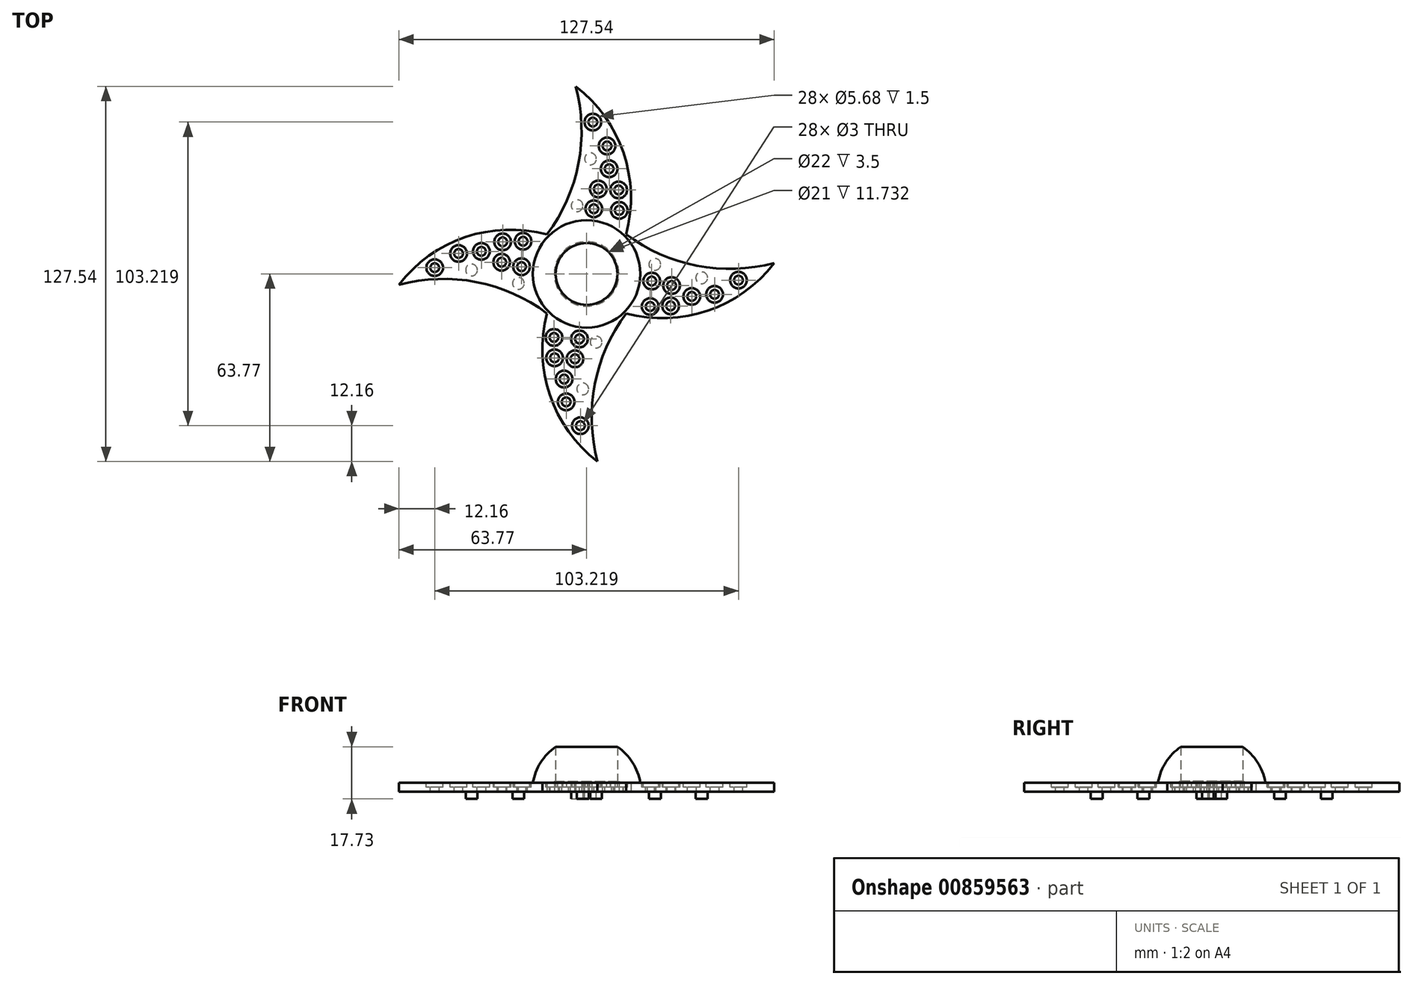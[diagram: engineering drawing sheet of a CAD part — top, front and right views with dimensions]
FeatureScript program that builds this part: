
annotation { "Feature Type Name" : "Feature", "Feature Type Description" : "" }
export const myFeature = defineFeature(function(context is Context, id is Id, definition is map)
    precondition{}
    {
        {
            var Q0;
            Q0=qCreatedBy(makeId("Top.planeOp"),FACE);
            var sketch = newSketch(context, id + "F0", { "sketchPlane" : qUnion([Q0])});
            skCircle(sketch, "E0", {"center": v(0, 0) * mm, "radius": 18.5 * mm});
            skLineSegment(sketch, "E1", {"start": v(0, 18.5) * mm, "end": v(0, -18.5) * mm});
            skSolve(sketch);
        }
        {
            var Q0;
            {var subQ0=sQuery(id+"F0.wireOp",EDGE,"E1");Q0=makeQuery(id+"F0.imprint","IMPRINT",FACE,{"disambiguationData":[TD([[makeQuery(id+"F0.imprint","IMPRINT",EDGE,{"derivedFrom":subQ0}),1.0]])]});}
            var Q1;
            Q1=sQuery(id+"F0.wireOp",EDGE,"E1");
            revolve(context, id + "F1", {"surfaceOperationType" : NewSurfaceOperationType.NEW, "entities" : qUnion([Q0]), "axis" : qUnion([Q1]), "revolveType" : RevolveType.ONE_DIRECTION, "angle" : 180 * degree});
        }
        {
            var Q0;
            Q0=makeQuery(id+"F1.opRevolve","CAP_FACE",FACE,{"disambiguationData":[OSD([sQuery(id+"F0.wireOp",EDGE,"E0"),sQuery(id+"F0.wireOp",EDGE,"E1")])],"isStart":true});
            var sketch = newSketch(context, id + "F2", { "sketchPlane" : qUnion([Q0])});
            skCircle(sketch, "E2", {"center": v(0, 0) * mm, "radius": 11 * mm});
            skSolve(sketch);
        }
        {
            var Q0;
            Q0 = qSketchRegion(id + "F2", true);
            extrude(context, id + "F3", {"entities" : qUnion([Q0]), "operationType" : NewBodyOperationType.REMOVE, "oppositeDirection" : true, "depth" : 3.5 * mm, "offsetDistance" : 25 * mm});
        }
        {
            var Q0;
            Q0=makeQuery(id+"F3.boolean.opBoolean","COPY",FACE,{"derivedFrom":makeQuery(id+"F3.opExtrude","CAP_FACE",FACE,{"disambiguationData":[OSD([sQuery(id+"F2.wireOp",EDGE,"E2")])],"isStart":false})});
            var sketch = newSketch(context, id + "F4", { "sketchPlane" : qUnion([Q0])});
            skCircle(sketch, "E3", {"center": v(0, 0) * mm, "radius": 10.5 * mm});
            skSolve(sketch);
        }
        {
            var Q0;
            Q0 = qSketchRegion(id + "F4", true);
            extrude(context, id + "F5", {"entities" : qUnion([Q0]), "operationType" : NewBodyOperationType.REMOVE, "surfaceOperationType" : NewSurfaceOperationType.ADD, "oppositeDirection" : true, "depth" : 25 * mm, "offsetDistance" : 25 * mm});
        }
        {
            var Q0;
            Q0=makeQuery(id+"F1.opRevolve","CAP_FACE",FACE,{"disambiguationData":[OSD([sQuery(id+"F0.wireOp",EDGE,"E0"),sQuery(id+"F0.wireOp",EDGE,"E1")])],"isStart":true});
            var sketch = newSketch(context, id + "F6", { "sketchPlane" : qUnion([Q0])});
            skCircle(sketch, "E4", {"center": v(0, 0) * mm, "radius": 17.5 * mm});
            skLineSegment(sketch, "E5", {"start": v(13.08, 13.08) * mm, "end": v(13.44, 13.44) * mm});
            skLineSegment(sketch, "E6", {"start": v(-13.08, 13.08) * mm, "end": v(-13.44, 13.44) * mm});
            skArc(sketch, "E7", {"start": v(3.7, 63.77) * mm, "mid": v(-12.5, 41.2) * mm, "end": v(-13.44, 13.44) * mm});
            skArc(sketch, "E8", {"start": v(3.7, 63.77) * mm, "mid": v(2.78, 37.48) * mm, "end": v(13.44, 13.44) * mm});
            skLineSegment(sketch, "E9.1.0", {"start": v(-13.08, -13.08) * mm, "end": v(-13.44, -13.44) * mm});
            skArc(sketch, "E9.1.1", {"start": v(-63.77, 3.7) * mm, "mid": v(-41.2, -12.5) * mm, "end": v(-13.44, -13.44) * mm});
            skArc(sketch, "E9.1.2", {"start": v(-63.77, 3.7) * mm, "mid": v(-37.48, 2.78) * mm, "end": v(-13.44, 13.44) * mm});
            skLineSegment(sketch, "E9.2.0", {"start": v(13.08, -13.08) * mm, "end": v(13.44, -13.44) * mm});
            skArc(sketch, "E9.2.1", {"start": v(-3.7, -63.77) * mm, "mid": v(12.5, -41.2) * mm, "end": v(13.44, -13.44) * mm});
            skArc(sketch, "E9.2.2", {"start": v(-3.7, -63.77) * mm, "mid": v(-2.78, -37.48) * mm, "end": v(-13.44, -13.44) * mm});
            skLineSegment(sketch, "E9.2.3", {"start": v(-13.08, -13.08) * mm, "end": v(-13.44, -13.44) * mm});
            skArc(sketch, "E9.3.1", {"start": v(63.77, -3.7) * mm, "mid": v(41.2, 12.5) * mm, "end": v(13.44, 13.44) * mm});
            skArc(sketch, "E9.3.2", {"start": v(63.77, -3.7) * mm, "mid": v(37.48, -2.78) * mm, "end": v(13.44, -13.44) * mm});
            skLineSegment(sketch, "E9.3.3", {"start": v(13.08, -13.08) * mm, "end": v(13.44, -13.44) * mm});
            skSolve(sketch);
        }
        {
            var Q0;
            Q0 = qSketchRegion(id + "F6", true);
            extrude(context, id + "F7", {"entities" : qUnion([Q0]), "operationType" : NewBodyOperationType.ADD, "oppositeDirection" : true, "depth" : 3 * mm, "offsetDistance" : 25 * mm});
        }
        {
            var Q0;
            Q0=makeQuery(id+"F7.opExtrude","CAP_FACE",FACE,{"disambiguationData":[OSD([sQuery(id+"F6.wireOp",EDGE,"E4"),sQuery(id+"F6.wireOp",EDGE,"E7"),sQuery(id+"F6.wireOp",EDGE,"E8"),sQuery(id+"F6.wireOp",EDGE,"E9.1.1"),sQuery(id+"F6.wireOp",EDGE,"E9.1.2"),sQuery(id+"F6.wireOp",EDGE,"E9.2.1"),sQuery(id+"F6.wireOp",EDGE,"E9.2.2"),sQuery(id+"F6.wireOp",EDGE,"E9.3.1"),sQuery(id+"F6.wireOp",EDGE,"E9.3.2")])],"isStart":false});
            var sketch = newSketch(context, id + "F8", { "sketchPlane" : qUnion([Q0])});
            skCircle(sketch, "E10", {"center": v(-11.08, -21.6) * mm, "radius": 2.84 * mm});
            skCircle(sketch, "E11", {"center": v(-2.44, -22.11) * mm, "radius": 2.84 * mm});
            skCircle(sketch, "E12", {"center": v(-10.9, -28.54) * mm, "radius": 2.84 * mm});
            skCircle(sketch, "E13", {"center": v(-3.96, -28.88) * mm, "radius": 2.84 * mm});
            skCircle(sketch, "E14", {"center": v(-7.66, -35.75) * mm, "radius": 2.84 * mm});
            skCircle(sketch, "E15", {"center": v(-6.94, -43.5) * mm, "radius": 2.84 * mm});
            skCircle(sketch, "E16", {"center": v(-2.12, -51.6) * mm, "radius": 2.84 * mm});
            skCircle(sketch, "E17.1.0", {"center": v(21.6, -11.08) * mm, "radius": 2.84 * mm});
            skCircle(sketch, "E17.1.1", {"center": v(22.11, -2.44) * mm, "radius": 2.84 * mm});
            skCircle(sketch, "E17.1.2", {"center": v(28.54, -10.9) * mm, "radius": 2.84 * mm});
            skCircle(sketch, "E17.1.3", {"center": v(28.88, -3.96) * mm, "radius": 2.84 * mm});
            skCircle(sketch, "E17.1.4", {"center": v(35.75, -7.66) * mm, "radius": 2.84 * mm});
            skCircle(sketch, "E17.1.5", {"center": v(43.5, -6.94) * mm, "radius": 2.84 * mm});
            skCircle(sketch, "E17.1.6", {"center": v(51.6, -2.12) * mm, "radius": 2.84 * mm});
            skCircle(sketch, "E17.2.0", {"center": v(11.08, 21.6) * mm, "radius": 2.84 * mm});
            skCircle(sketch, "E17.2.1", {"center": v(2.44, 22.11) * mm, "radius": 2.84 * mm});
            skCircle(sketch, "E17.2.2", {"center": v(10.9, 28.54) * mm, "radius": 2.84 * mm});
            skCircle(sketch, "E17.2.3", {"center": v(3.96, 28.88) * mm, "radius": 2.84 * mm});
            skCircle(sketch, "E17.2.4", {"center": v(7.66, 35.75) * mm, "radius": 2.84 * mm});
            skCircle(sketch, "E17.2.5", {"center": v(6.94, 43.5) * mm, "radius": 2.84 * mm});
            skCircle(sketch, "E17.2.6", {"center": v(2.12, 51.6) * mm, "radius": 2.84 * mm});
            skCircle(sketch, "E17.3.0", {"center": v(-21.6, 11.08) * mm, "radius": 2.84 * mm});
            skCircle(sketch, "E17.3.1", {"center": v(-22.11, 2.44) * mm, "radius": 2.84 * mm});
            skCircle(sketch, "E17.3.2", {"center": v(-28.54, 10.9) * mm, "radius": 2.84 * mm});
            skCircle(sketch, "E17.3.3", {"center": v(-28.88, 3.96) * mm, "radius": 2.84 * mm});
            skCircle(sketch, "E17.3.4", {"center": v(-35.75, 7.66) * mm, "radius": 2.84 * mm});
            skCircle(sketch, "E17.3.5", {"center": v(-43.5, 6.94) * mm, "radius": 2.84 * mm});
            skCircle(sketch, "E17.3.6", {"center": v(-51.6, 2.12) * mm, "radius": 2.84 * mm});
            skPoint(sketch, "E17.center", {"position": v(0, 0) * mm});
            skSolve(sketch);
        }
        {
            var Q0;
            Q0 = qSketchRegion(id + "F8", true);
            extrude(context, id + "F9", {"entities" : qUnion([Q0]), "operationType" : NewBodyOperationType.REMOVE, "oppositeDirection" : true, "depth" : 1.5 * mm, "offsetDistance" : 25 * mm});
        }
        {
            var Q0;
            Q0=makeQuery(id+"F7.opExtrude","CAP_FACE",FACE,{"disambiguationData":[OSD([sQuery(id+"F6.wireOp",EDGE,"E4"),sQuery(id+"F6.wireOp",EDGE,"E7"),sQuery(id+"F6.wireOp",EDGE,"E8"),sQuery(id+"F6.wireOp",EDGE,"E9.1.1"),sQuery(id+"F6.wireOp",EDGE,"E9.1.2"),sQuery(id+"F6.wireOp",EDGE,"E9.2.1"),sQuery(id+"F6.wireOp",EDGE,"E9.2.2"),sQuery(id+"F6.wireOp",EDGE,"E9.3.1"),sQuery(id+"F6.wireOp",EDGE,"E9.3.2")])],"isStart":false});
            var sketch = newSketch(context, id + "F10", { "sketchPlane" : qUnion([Q0])});
            skCircle(sketch, "E18", {"center": v(-2.44, -22.11) * mm, "radius": 1.5 * mm});
            skCircle(sketch, "E19", {"center": v(-22.11, 2.44) * mm, "radius": 1.5 * mm});
            skCircle(sketch, "E20", {"center": v(2.44, 22.11) * mm, "radius": 1.5 * mm});
            skCircle(sketch, "E21", {"center": v(22.11, -2.44) * mm, "radius": 1.5 * mm});
            skCircle(sketch, "E22", {"center": v(-11.08, -21.6) * mm, "radius": 1.5 * mm});
            skCircle(sketch, "E23", {"center": v(-10.9, -28.54) * mm, "radius": 1.5 * mm});
            skCircle(sketch, "E24", {"center": v(-3.96, -28.88) * mm, "radius": 1.5 * mm});
            skCircle(sketch, "E25", {"center": v(-7.66, -35.75) * mm, "radius": 1.5 * mm});
            skCircle(sketch, "E26", {"center": v(-6.94, -43.5) * mm, "radius": 1.5 * mm});
            skCircle(sketch, "E27", {"center": v(-2.12, -51.6) * mm, "radius": 1.5 * mm});
            skCircle(sketch, "E28.1.0", {"center": v(21.6, -11.08) * mm, "radius": 1.5 * mm});
            skCircle(sketch, "E28.1.1", {"center": v(28.54, -10.9) * mm, "radius": 1.5 * mm});
            skCircle(sketch, "E28.1.2", {"center": v(28.88, -3.96) * mm, "radius": 1.5 * mm});
            skCircle(sketch, "E28.1.4", {"center": v(35.75, -7.66) * mm, "radius": 1.5 * mm});
            skCircle(sketch, "E28.1.5", {"center": v(43.5, -6.94) * mm, "radius": 1.5 * mm});
            skCircle(sketch, "E28.1.6", {"center": v(51.6, -2.12) * mm, "radius": 1.5 * mm});
            skCircle(sketch, "E28.2.0", {"center": v(11.08, 21.6) * mm, "radius": 1.5 * mm});
            skCircle(sketch, "E28.2.1", {"center": v(10.9, 28.54) * mm, "radius": 1.5 * mm});
            skCircle(sketch, "E28.2.2", {"center": v(3.96, 28.88) * mm, "radius": 1.5 * mm});
            skCircle(sketch, "E28.2.4", {"center": v(7.66, 35.75) * mm, "radius": 1.5 * mm});
            skCircle(sketch, "E28.2.5", {"center": v(6.94, 43.5) * mm, "radius": 1.5 * mm});
            skCircle(sketch, "E28.2.6", {"center": v(2.12, 51.6) * mm, "radius": 1.5 * mm});
            skCircle(sketch, "E28.3.0", {"center": v(-21.6, 11.08) * mm, "radius": 1.5 * mm});
            skCircle(sketch, "E28.3.1", {"center": v(-28.54, 10.9) * mm, "radius": 1.5 * mm});
            skCircle(sketch, "E28.3.2", {"center": v(-28.88, 3.96) * mm, "radius": 1.5 * mm});
            skCircle(sketch, "E28.3.4", {"center": v(-35.75, 7.66) * mm, "radius": 1.5 * mm});
            skCircle(sketch, "E28.3.5", {"center": v(-43.5, 6.94) * mm, "radius": 1.5 * mm});
            skCircle(sketch, "E28.3.6", {"center": v(-51.6, 2.12) * mm, "radius": 1.5 * mm});
            skPoint(sketch, "E28.center", {"position": v(0, 0) * mm});
            skSolve(sketch);
        }
        {
            var Q0;
            Q0 = qSketchRegion(id + "F10", true);
            extrude(context, id + "F11", {"entities" : qUnion([Q0]), "operationType" : NewBodyOperationType.REMOVE, "oppositeDirection" : true, "depth" : 25 * mm, "offsetDistance" : 25 * mm});
        }
        {
            var Q0;
            Q0=makeQuery(id+"F7.opExtrude","CAP_FACE",FACE,{"disambiguationData":[OSD([sQuery(id+"F6.wireOp",EDGE,"E4"),sQuery(id+"F6.wireOp",EDGE,"E7"),sQuery(id+"F6.wireOp",EDGE,"E8"),sQuery(id+"F6.wireOp",EDGE,"E9.1.1"),sQuery(id+"F6.wireOp",EDGE,"E9.1.2"),sQuery(id+"F6.wireOp",EDGE,"E9.2.1"),sQuery(id+"F6.wireOp",EDGE,"E9.2.2"),sQuery(id+"F6.wireOp",EDGE,"E9.3.1"),sQuery(id+"F6.wireOp",EDGE,"E9.3.2")])],"isStart":true});
            var sketch = newSketch(context, id + "F12", { "sketchPlane" : qUnion([Q0])});
            skCircle(sketch, "E29", {"center": v(-23.18, 3.23) * mm, "radius": 2 * mm});
            skCircle(sketch, "E30", {"center": v(-39.1, -1.31) * mm, "radius": 2 * mm});
            skCircle(sketch, "E31.1.0", {"center": v(-3.23, -23.18) * mm, "radius": 2 * mm});
            skCircle(sketch, "E31.1.1", {"center": v(1.31, -39.1) * mm, "radius": 2 * mm});
            skCircle(sketch, "E31.2.0", {"center": v(23.18, -3.23) * mm, "radius": 2 * mm});
            skCircle(sketch, "E31.2.1", {"center": v(39.1, 1.31) * mm, "radius": 2 * mm});
            skCircle(sketch, "E31.3.0", {"center": v(3.23, 23.18) * mm, "radius": 2 * mm});
            skCircle(sketch, "E31.3.1", {"center": v(-1.31, 39.1) * mm, "radius": 2 * mm});
            skPoint(sketch, "E31.center", {"position": v(0, 0) * mm});
            skSolve(sketch);
        }
        {
            var Q0;
            Q0 = qSketchRegion(id + "F12", true);
            extrude(context, id + "F13", {"entities" : qUnion([Q0]), "operationType" : NewBodyOperationType.ADD, "depth" : 2.5 * mm, "offsetDistance" : 25 * mm});
        }
    });
